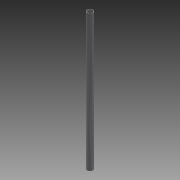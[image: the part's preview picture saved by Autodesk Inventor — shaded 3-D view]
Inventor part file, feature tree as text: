
AUTODESK INVENTOR PART (.ipt)
format: ipt  version: 2013 (Build 170138000, 138)  size: 66,048 bytes
history: native  units: in
note: dims shown in document units (in); Inventor stores cm internally (conversion verified against a paired STEP export)
features: extrude x1, sketch x1
ambient origin geometry x8: Origin, YZ Plane, XZ Plane, XY Plane, X Axis, Y Axis, Z Axis, Center Point
bodies: Solid1 (feature_tree)
feature tree (2):
  extrude  "Extrusion1"  Depth=0.1in
  sketch  "Sketch1"  dims[d0=2.0in d2=0.1in d3=48.0in d4=0.0in]
